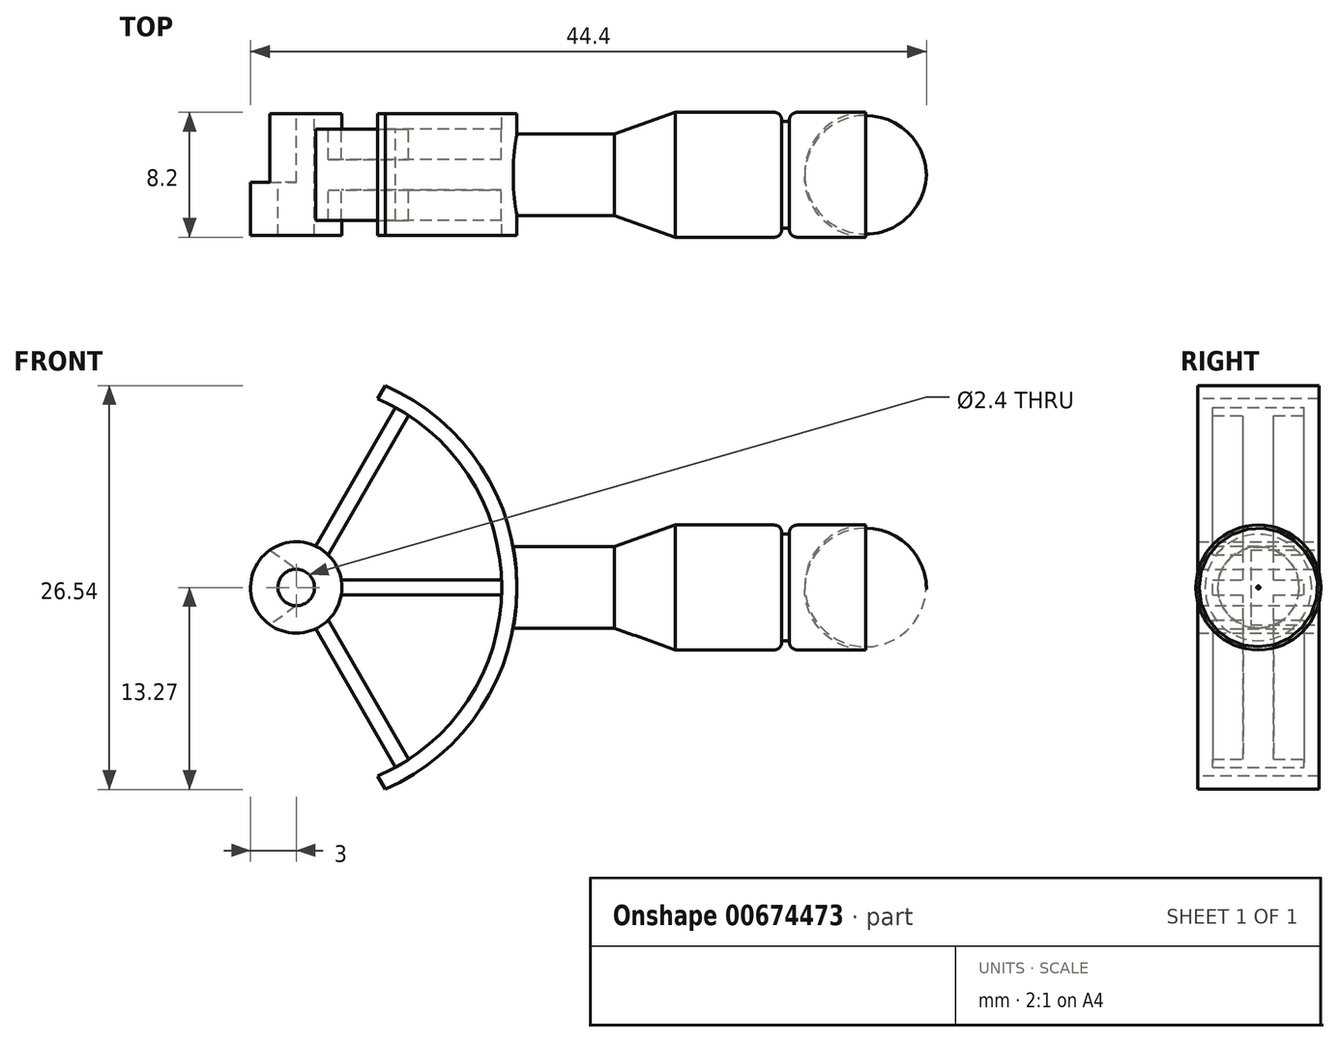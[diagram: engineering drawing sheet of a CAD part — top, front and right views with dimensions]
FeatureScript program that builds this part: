
annotation { "Feature Type Name" : "Feature", "Feature Type Description" : "" }
export const myFeature = defineFeature(function(context is Context, id is Id, definition is map)
    precondition{}
    {
        {
            var Q0;
            Q0=qCreatedBy(makeId("Top.planeOp"),FACE);
            var sketch = newSketch(context, id + "F0", { "sketchPlane" : qUnion([Q0])});
            skLineSegment(sketch, "E0", {"start": v(0, 2.67) * mm, "end": v(0, 0) * mm});
            skLineSegment(sketch, "E1", {"start": v(0, 2.67) * mm, "end": v(7.4, 2.68) * mm});
            skLineSegment(sketch, "E2", {"start": v(7.4, 2.68) * mm, "end": v(11.4, 4.1) * mm});
            skLineSegment(sketch, "E3", {"start": v(11.4, 4.1) * mm, "end": v(18.4, 4.1) * mm});
            skLineSegment(sketch, "E4", {"start": v(18.4, 4.1) * mm, "end": v(18.4, 3.5) * mm});
            skLineSegment(sketch, "E5", {"start": v(18.4, 3.5) * mm, "end": v(18.9, 3.5) * mm});
            skLineSegment(sketch, "E6", {"start": v(18.9, 3.5) * mm, "end": v(18.9, 4.1) * mm});
            skLineSegment(sketch, "E7", {"start": v(18.9, 4.1) * mm, "end": v(27.9, 4.1) * mm});
            skLineSegment(sketch, "E8", {"start": v(27.9, 4.1) * mm, "end": v(27.9, 0) * mm});
            skLineSegment(sketch, "E9", {"start": v(27.9, 0) * mm, "end": v(0, 0) * mm});
            skSolve(sketch);
        }
        {
            var Q0;
            Q0 = qSketchRegion(id + "F0", true);
            var Q1;
            Q1=sQuery(id+"F0.wireOp",EDGE,"E9");
            revolve(context, id + "F1", {"entities" : qUnion([Q0]), "axis" : qUnion([Q1]), "revolveType" : RevolveType.FULL});
        }
        {
            var Q0;
            Q0=makeQuery(id+"F1.opRevolve","SWEPT_EDGE",EDGE,{"disambiguationData":[OSD([sQuery(id+"F0.wireOp",EDGE,"E7"),sQuery(id+"F0.wireOp",EDGE,"E8")])]});
            fillet(context, id + "F2", {"entities" : qUnion([Q0]), "radius" : 4 * mm, "tangentPropagation" : true, "allowEdgeOverflow" : false});
        }
        {
            var Q0;
            Q0=makeQuery(id+"F1.opRevolve","SWEPT_EDGE",EDGE,{"disambiguationData":[OSD([sQuery(id+"F0.wireOp",EDGE,"E3"),sQuery(id+"F0.wireOp",EDGE,"E4")])]});
            var Q1;
            Q1=makeQuery(id+"F1.opRevolve","SWEPT_EDGE",EDGE,{"disambiguationData":[OSD([sQuery(id+"F0.wireOp",EDGE,"E6"),sQuery(id+"F0.wireOp",EDGE,"E7")])]});
            fillet(context, id + "F3", {"entities" : qUnion([Q0, Q1]), "radius" : 0.5 * mm, "tangentPropagation" : true, "allowEdgeOverflow" : false});
        }
        {
            var Q0;
            Q0=qCreatedBy(makeId("Front.planeOp"),FACE);
            var sketch = newSketch(context, id + "F4", { "sketchPlane" : qUnion([Q0])});
            skCircle(sketch, "E10", {"center": v(-13.5, 0) * mm, "radius": 14.5 * mm});
            skCircle(sketch, "E11.0", {"center": v(-13.5, 0) * mm, "radius": 13.5 * mm});
            skSolve(sketch);
        }
        {
            var Q0;
            Q0 = qSketchRegion(id + "F4", true);
            extrude(context, id + "F5", {"entities" : qUnion([Q0]), "operationType" : NewBodyOperationType.ADD, "depth" : 4 * mm, "offsetDistance" : 25 * mm, "hasSecondDirection" : true, "secondDirectionOppositeDirection" : true, "secondDirectionDepth" : 4 * mm});
        }
        {
            var Q0;
            Q0=qCreatedBy(makeId("Front.planeOp"),FACE);
            var sketch = newSketch(context, id + "F6", { "sketchPlane" : qUnion([Q0])});
            skArc(sketch, "E12.0", {"start": v(0, -0.5) * mm, "mid": v(0, 0) * mm, "end": v(0, 0.5) * mm});
            skLineSegment(sketch, "E13", {"start": v(0, -0.5) * mm, "end": v(-10.54, -0.5) * mm});
            skLineSegment(sketch, "E14", {"start": v(-10.54, 0.5) * mm, "end": v(0, 0.5) * mm});
            skLineSegment(sketch, "E15", {"start": v(-11.4, 2.14) * mm, "end": v(-6.11, 11.3) * mm});
            skLineSegment(sketch, "E16.MirrorCS", {"start": v(-11.4, -2.14) * mm, "end": v(-6.11, -11.3) * mm});
            skLineSegment(sketch, "E17.MirrorCS", {"start": v(-12.22, -2.71) * mm, "end": v(-6.97, -11.81) * mm});
            skArc(sketch, "E18.trimOffspring", {"start": v(-6.97, -11.81) * mm, "mid": v(-6.53, -11.56) * mm, "end": v(-6.11, -11.3) * mm});
            skArc(sketch, "E19.trimOffspring", {"start": v(-6.11, 11.3) * mm, "mid": v(-6.53, 11.56) * mm, "end": v(-6.97, 11.81) * mm});
            skArc(sketch, "E20", {"start": v(-12.22, 2.71) * mm, "mid": v(-16.5, 0) * mm, "end": v(-12.22, -2.71) * mm});
            skCircle(sketch, "E21", {"center": v(-13.5, 0) * mm, "radius": 1.2 * mm});
            skPoint(sketch, "E22.orphan", {"position": v(-13.5, -0.5) * mm});
            skPoint(sketch, "E23.orphan", {"position": v(-12.35, -0.5) * mm});
            skPoint(sketch, "E24.orphan", {"position": v(-12.35, 0.5) * mm});
            skLineSegment(sketch, "E25.trimOffspring", {"start": v(-12.22, 2.71) * mm, "end": v(-6.97, 11.81) * mm});
            skPoint(sketch, "E26.start.orphan", {"position": v(-13.5, 0.5) * mm});
            skArc(sketch, "E27.trimOffspring", {"start": v(-10.54, 0.5) * mm, "mid": v(-10.84, 1.39) * mm, "end": v(-11.4, 2.14) * mm});
            skArc(sketch, "E28.trimOffspring", {"start": v(-11.4, -2.14) * mm, "mid": v(-10.84, -1.39) * mm, "end": v(-10.54, -0.5) * mm});
            skSolve(sketch);
        }
        {
            var Q0;
            Q0 = qSketchRegion(id + "F6", true);
            extrude(context, id + "F7", {"entities" : qUnion([Q0]), "operationType" : NewBodyOperationType.ADD, "depth" : 3 * mm, "offsetDistance" : 25 * mm, "hasSecondDirection" : true, "secondDirectionOppositeDirection" : true, "secondDirectionDepth" : 3 * mm});
        }
        {
            var Q0;
            Q0=makeQuery(id+"F7.opExtrude","CAP_FACE",FACE,{"disambiguationData":[OSD([sQuery(id+"F6.wireOp",EDGE,"E13"),sQuery(id+"F6.wireOp",EDGE,"E14"),sQuery(id+"F6.wireOp",EDGE,"E12.0"),sQuery(id+"F6.wireOp",EDGE,"E15"),sQuery(id+"F6.wireOp",EDGE,"E16.MirrorCS"),sQuery(id+"F6.wireOp",EDGE,"E17.MirrorCS"),sQuery(id+"F6.wireOp",EDGE,"E18.trimOffspring"),sQuery(id+"F6.wireOp",EDGE,"E19.trimOffspring"),sQuery(id+"F6.wireOp",EDGE,"E20"),sQuery(id+"F6.wireOp",EDGE,"E21"),sQuery(id+"F6.wireOp",EDGE,"E25.trimOffspring"),sQuery(id+"F6.wireOp",EDGE,"E27.trimOffspring"),sQuery(id+"F6.wireOp",EDGE,"E28.trimOffspring")])],"isStart":true});
            var sketch = newSketch(context, id + "F8", { "sketchPlane" : qUnion([Q0])});
            skArc(sketch, "E29.0", {"start": v(12.22, 2.71) * mm, "mid": v(16.5, 0) * mm, "end": v(12.22, -2.71) * mm});
            skArc(sketch, "E30.0", {"start": v(10.54, 0.5) * mm, "mid": v(10.84, 1.39) * mm, "end": v(11.4, 2.14) * mm});
            skCircle(sketch, "E31", {"center": v(13.5, 0) * mm, "radius": 3 * mm});
            skCircle(sketch, "E32.0", {"center": v(13.5, 0) * mm, "radius": 1.2 * mm});
            skSolve(sketch);
        }
        {
            var Q0;
            Q0 = qSketchRegion(id + "F8", true);
            extrude(context, id + "F9", {"entities" : qUnion([Q0]), "operationType" : NewBodyOperationType.ADD, "depth" : 1 * mm, "offsetDistance" : 25 * mm, "hasSecondDirection" : true, "secondDirectionOppositeDirection" : true, "secondDirectionDepth" : 7 * mm});
        }
        {
            var Q0;
            Q0=qCreatedBy(makeId("Front.planeOp"),FACE);
            var sketch = newSketch(context, id + "F10", { "sketchPlane" : qUnion([Q0])});
            skCircle(sketch, "E33.0", {"center": v(-13.5, 0) * mm, "radius": 13.5 * mm});
            skCircle(sketch, "E34.0", {"center": v(-13.5, 0) * mm, "radius": 1.2 * mm});
            skSolve(sketch);
        }
        {
            var Q0;
            Q0 = qSketchRegion(id + "F10", true);
            extrude(context, id + "F11", {"entities" : qUnion([Q0]), "operationType" : NewBodyOperationType.ADD, "depth" : 1 * mm, "offsetDistance" : 25 * mm, "hasSecondDirection" : true, "secondDirectionOppositeDirection" : true, "secondDirectionDepth" : 1 * mm});
        }
        {
            var Q0;
            Q0=qCreatedBy(makeId("Front.planeOp"),FACE);
            var sketch = newSketch(context, id + "F12", { "sketchPlane" : qUnion([Q0])});
            skLineSegment(sketch, "E35.0", {"start": v(-12.22, 2.71) * mm, "end": v(-6.97, 11.81) * mm});
            skArc(sketch, "E36.0", {"start": v(-6.97, 11.81) * mm, "mid": v(-7.55, 12.12) * mm, "end": v(-8.15, 12.4) * mm});
            skLineSegment(sketch, "E37.0", {"start": v(-12.22, -2.71) * mm, "end": v(-6.97, -11.81) * mm});
            skArc(sketch, "E38.0", {"start": v(-7.64, 13.27) * mm, "mid": v(-28, 0) * mm, "end": v(-7.64, -13.27) * mm});
            skLineSegment(sketch, "E39", {"start": v(-8.15, -12.4) * mm, "end": v(-7.64, -13.27) * mm});
            skLineSegment(sketch, "E40", {"start": v(-8.15, 12.4) * mm, "end": v(-7.64, 13.27) * mm});
            skArc(sketch, "E41.trimOffspring", {"start": v(-8.15, -12.4) * mm, "mid": v(-7.55, -12.12) * mm, "end": v(-6.97, -11.81) * mm});
            skArc(sketch, "E42", {"start": v(-12.22, 2.71) * mm, "mid": v(-16.5, 0) * mm, "end": v(-12.22, -2.71) * mm});
            skSolve(sketch);
        }
        {
            var Q0;
            Q0 = qSketchRegion(id + "F12", true);
            extrude(context, id + "F13", {"entities" : qUnion([Q0]), "operationType" : NewBodyOperationType.REMOVE, "oppositeDirection" : true, "depth" : 25 * mm, "offsetDistance" : 25 * mm, "hasSecondDirection" : true, "secondDirectionOppositeDirection" : false, "secondDirectionDepth" : 25 * mm});
        }
        {
            var Q0;
            Q0=makeQuery(id+"F9.opExtrude","CAP_FACE",FACE,{"disambiguationData":[OSD([sQuery(id+"F8.wireOp",EDGE,"E31"),sQuery(id+"F8.wireOp",EDGE,"E32.0")])],"isStart":false});
            var sketch = newSketch(context, id + "F14", { "sketchPlane" : qUnion([Q0])});
            skLineSegment(sketch, "E43", {"start": v(15.22, 2.46) * mm, "end": v(13.48, 1.2) * mm});
            skLineSegment(sketch, "E44", {"start": v(13.48, -1.2) * mm, "end": v(15.22, -2.46) * mm});
            skArc(sketch, "E45.0", {"start": v(13.48, -1.2) * mm, "mid": v(14.7, 0) * mm, "end": v(13.48, 1.2) * mm});
            skArc(sketch, "E46.0", {"start": v(15.22, -2.46) * mm, "mid": v(16.5, 0) * mm, "end": v(15.22, 2.46) * mm});
            skSolve(sketch);
        }
        {
            var Q0;
            Q0 = qSketchRegion(id + "F14", true);
            extrude(context, id + "F15", {"entities" : qUnion([Q0]), "operationType" : NewBodyOperationType.REMOVE, "oppositeDirection" : true, "depth" : 4.5 * mm, "offsetDistance" : 25 * mm});
        }
    });
